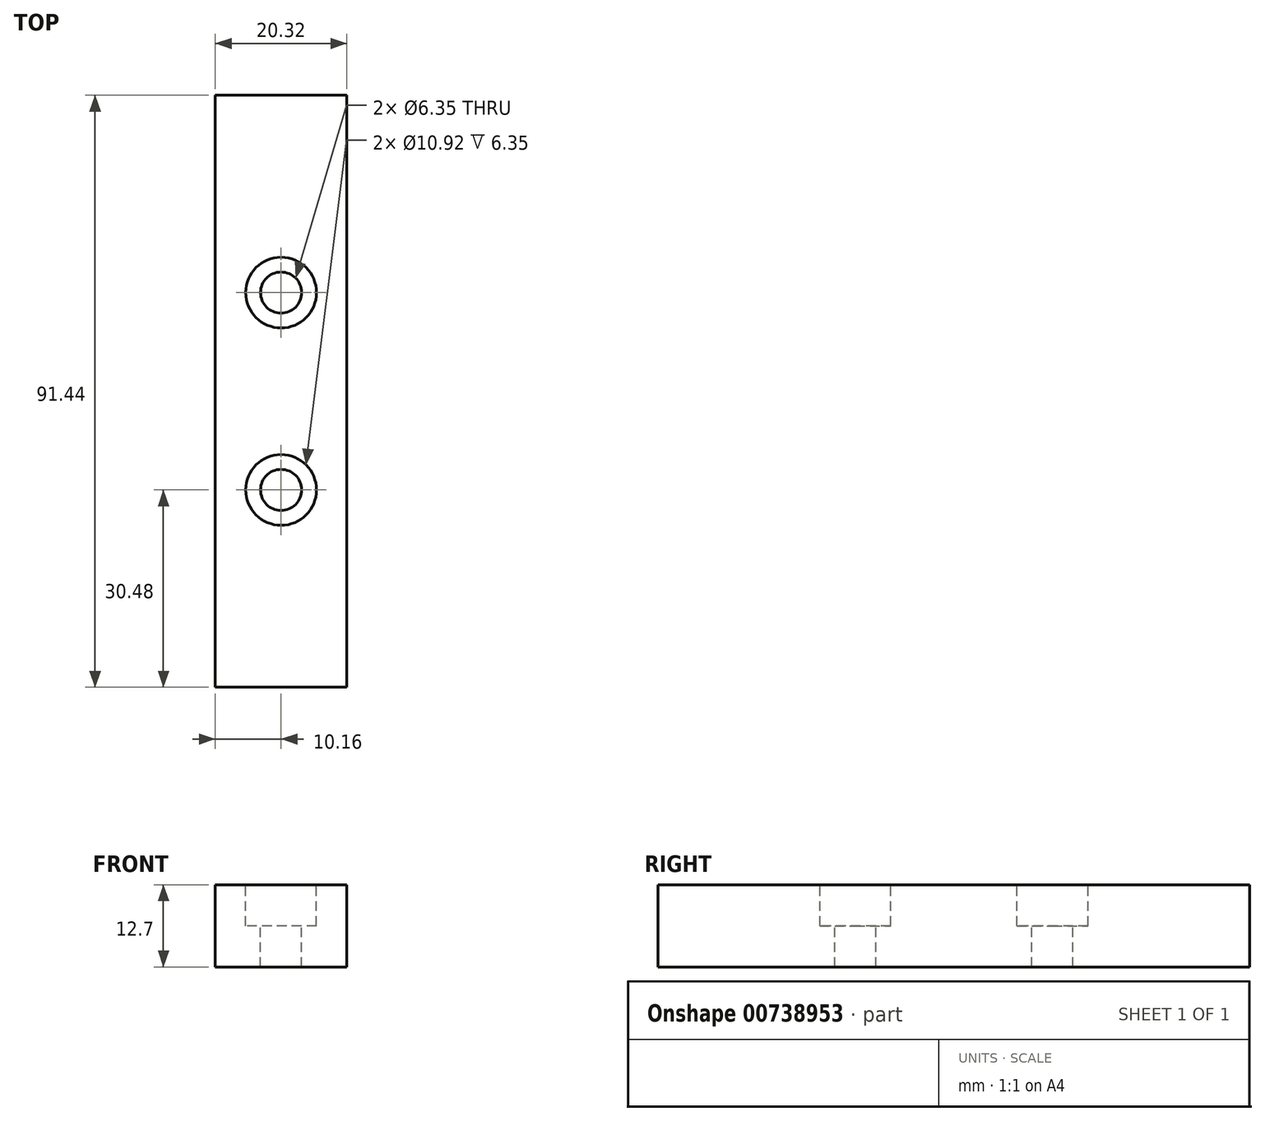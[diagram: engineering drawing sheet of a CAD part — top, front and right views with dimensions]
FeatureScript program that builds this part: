
annotation { "Feature Type Name" : "Feature", "Feature Type Description" : "" }
export const myFeature = defineFeature(function(context is Context, id is Id, definition is map)
    precondition{}
    {
        {
            var Q0;
            Q0=qCreatedBy(makeId("Top.planeOp"),FACE);
            var sketch = newSketch(context, id + "F0", { "sketchPlane" : qUnion([Q0])});
            skLineSegment(sketch, "E0.bottom", {"start": v(10.16, -45.72) * mm, "end": v(-10.16, -45.72) * mm});
            skLineSegment(sketch, "E0.top", {"start": v(10.16, 45.72) * mm, "end": v(-10.16, 45.72) * mm});
            skLineSegment(sketch, "E0.left", {"start": v(10.16, -45.72) * mm, "end": v(10.16, 45.72) * mm});
            skLineSegment(sketch, "E0.right", {"start": v(-10.16, -45.72) * mm, "end": v(-10.16, 45.72) * mm});
            skPoint(sketch, "E0.middle", {"position": v(0, 0) * mm});
            skSolve(sketch);
        }
        {
            var Q0;
            Q0=makeQuery(id+"F0.imprint","IMPRINT",FACE,{"disambiguationData":[TD([[makeQuery(id+"F0.imprint","IMPRINT",EDGE,{"derivedFrom":sQuery(id+"F0.wireOp",EDGE,"E0.bottom")}),-1.0]])]});
            extrude(context, id + "F1", {"entities" : qUnion([Q0]), "depth" : 12.7 * mm, "offsetDistance" : 25.4 * mm});
        }
        {
            var Q0;
            Q0=makeQuery(id+"F1.opExtrude","CAP_FACE",FACE,{"disambiguationData":[OSD([sQuery(id+"F0.wireOp",EDGE,"E0.bottom"),sQuery(id+"F0.wireOp",EDGE,"E0.top"),sQuery(id+"F0.wireOp",EDGE,"E0.left"),sQuery(id+"F0.wireOp",EDGE,"E0.right")])],"isStart":false});
            var sketch = newSketch(context, id + "F2", { "sketchPlane" : qUnion([Q0])});
            skPoint(sketch, "E1", {"position": v(0, 15.24) * mm});
            skPoint(sketch, "E2", {"position": v(0, -15.24) * mm});
            skLineSegment(sketch, "E3", {"start": v(0, -45.72) * mm, "end": v(0, -15.24) * mm});
            skLineSegment(sketch, "E4", {"start": v(0, 15.24) * mm, "end": v(0, 45.72) * mm});
            skLineSegment(sketch, "E5", {"start": v(0, 15.24) * mm, "end": v(0, -15.24) * mm});
            skSolve(sketch);
        }
        {
            var Q0;
            Q0=sQuery(id+"F2.wireOp",VERTEX,"E1");
            var Q1;
            Q1=sQuery(id+"F2.wireOp",VERTEX,"E2");
            var Q2;
            Q2=makeQuery(id+"F1.opExtrude","SWEPT_BODY",BODY,{"disambiguationData":[OSD([sQuery(id+"F0.wireOp",EDGE,"E0.bottom"),sQuery(id+"F0.wireOp",EDGE,"E0.top"),sQuery(id+"F0.wireOp",EDGE,"E0.left"),sQuery(id+"F0.wireOp",EDGE,"E0.right")])]});
            hole(context, id + "F3", {"style" : HoleStyle.C_BORE, "endStyle" : HoleEndStyle.THROUGH, "holeDiameter" : 6.35 * mm, "cBoreDiameter" : 10.92 * mm, "cBoreDepth" : 6.35 * mm, "majorDiameter" : 6.35 * mm, "isTappedThrough" : true, "tappedDepth" : 12.7 * mm, "tapClearance" : 3, "locations" : qUnion([Q0, Q1]), "scope" : qUnion([Q2])});
        }
    });
